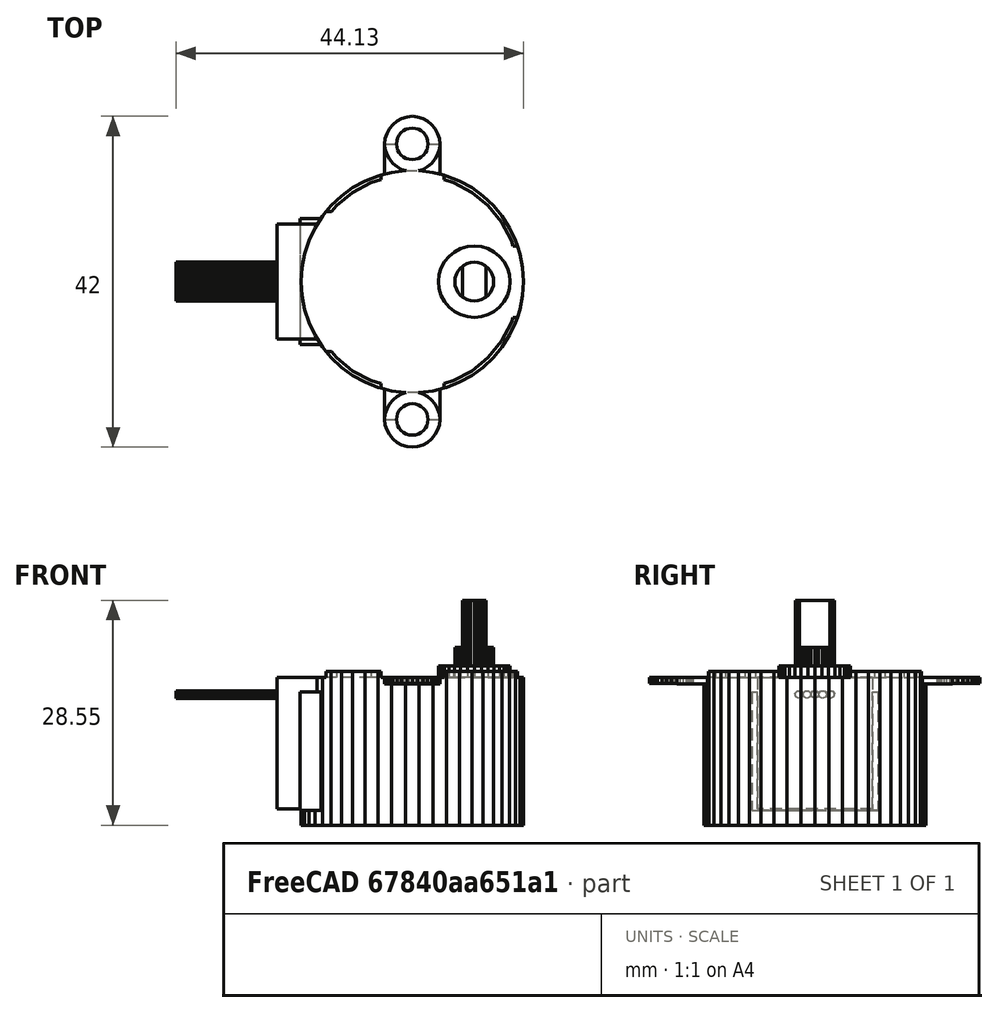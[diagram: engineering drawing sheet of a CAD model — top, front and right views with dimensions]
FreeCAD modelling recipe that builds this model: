
FCSTD DOCUMENT  (FreeCAD 0.14R3692 (Git))
Label: StepMotor_28BYJ-48
License: CC-BY 3.0
LicenseURL: http://creativecommons.org/licenses/by/3.0/
objects: Part::Prism×14, Part::Box×8, Part::MultiFuse×3, Part::Cut×3, Part::Fuse×3, Part::Feature×1
note: 32 computed .brp shape members not serialized (recipe doc carries the construction recipe); baked Part::Feature solids carry a one-line shape summary decoded from their .brp

FEATURE [Part::Prism] prism
  Circumradius = 14.125
  Height = 0.75
  Placement = pos=(0,0,-0.375) rot=(0,0,1;0rad)
  Polygon = 50
FEATURE [Part::Prism] prism001
  Circumradius = 13.625
  Height = 0.8
  Placement = pos=(0,0,-0.4) rot=(0,0,1;0rad)
  Polygon = 32
FEATURE [Part::Box] cube
  Height = 1.4
  Length = 8
  Placement = pos=(-4,-17.5,-0.7) rot=(0,0,1;0rad)
  Width = 35
FEATURE [Part::Box] cube001
  Height = 1.4
  Length = 30.25
  Placement = pos=(-15.125,-4.55,-0.7) rot=(0,0,1;0rad)
  Width = 9.1
FEATURE [Part::Box] cube002
  Height = 1.4
  Length = 28.25
  Placement = pos=(-28.25,-8.9,-0.7) rot=(0,0,1;0rad)
  Width = 17.8
FEATURE [Part::MultiFuse] union
  Shapes = -> [prism001,cube,cube001,cube002]
FEATURE [Part::Cut] difference
  Base = -> prism
  Placement = pos=(0,0,-9.75) rot=(0,0,1;0rad)
  Tool = -> union
FEATURE [Part::Prism] prism002
  Circumradius = 14.125
  Height = 18.8
  Placement = pos=(0,0,-9.4) rot=(0,0,1;0rad)
  Polygon = 50
FEATURE [Part::Prism] prism003
  Circumradius = 4.55
  Height = 18.8
  Placement = pos=(7.875,0,-10.85) rot=(0,0,1;0rad)
  Polygon = 32
FEATURE [Part::Prism] prism004
  Circumradius = 2.465
  Height = 18.8
  Placement = pos=(0,0,-9.4) rot=(0,0,1;0rad)
  Polygon = 32
FEATURE [Part::Box] cube003
  Height = 6
  Length = 4.93
  Placement = pos=(1.5,-2.465,-9.425) rot=(0,0,1;0rad)
  Width = 4.93
FEATURE [Part::Box] cube004
  Height = 6
  Length = 4.93
  Placement = pos=(-6.43,-2.465,-9.425) rot=(0,0,1;0rad)
  Width = 4.93
FEATURE [Part::Fuse] union001
  Base = -> cube003
  Tool = -> cube004
FEATURE [Part::Cut] difference001
  Base = -> prism004
  Placement = pos=(7.875,0,-9.75) rot=(0,0,1;0rad)
  Tool = -> union001
FEATURE [Part::Box] cube005
  Height = 0.8
  Length = 7
  Placement = pos=(-3.5,-17.5,-9.375) rot=(0,0,1;0rad)
  Width = 35
FEATURE [Part::Prism] prism005
  Circumradius = 3.5
  Height = 0.8
  Placement = pos=(0,17.5,-9.4) rot=(0,0,1;0rad)
  Polygon = 32
FEATURE [Part::Prism] prism006
  Circumradius = 3.5
  Height = 0.8
  Placement = pos=(0,-17.5,-9.4) rot=(0,0,1;0rad)
  Polygon = 32
FEATURE [Part::Box] cube006
  Height = 16.7
  Length = 28.25
  Placement = pos=(-17.175,-7.3,-9.35) rot=(0,0,1;0rad)
  Width = 14.6
FEATURE [Part::Box] cube007
  Height = 15
  Length = 24.5
  Placement = pos=(-14.25,-8,-7.5) rot=(0,0,1;0rad)
  Width = 16
FEATURE [Part::MultiFuse] union002
  Shapes = -> [difference,prism002,prism003,difference001,cube005,prism005,prism006,cube006,cube007]
FEATURE [Part::Prism] prism007
  Circumradius = 2
  Height = 2
  Placement = pos=(0,17.5,-10.4) rot=(0,0,1;0rad)
  Polygon = 32
FEATURE [Part::Prism] prism008
  Circumradius = 2
  Height = 2
  Placement = pos=(0,-17.5,-10.4) rot=(0,0,1;0rad)
  Polygon = 32
FEATURE [Part::Fuse] union003
  Base = -> prism007
  Tool = -> prism008
FEATURE [Part::Cut] difference002
  Base = -> union002
  Tool = -> union003
FEATURE [Part::Prism] prism009 .. prism013  x5 (patterned run collapsed; names and placements below)
  Circumradius = 0.5
  Height = 30
  Polygon = 7
  placements: 5 in arithmetic series — first pos=(0,2,0) rot=(0,0,1;0rad), step (0,-1,0), last pos=(0,-2,0) rot=(0,0,1;0rad)
FEATURE [Part::MultiFuse] Group
  Placement = pos=(0,0,-7.2) rot=(0,-1,0;1.5708rad)
  Shapes = -> [prism009,prism010,prism011,prism012,prism013]
FEATURE [Part::Fuse] Matrix_Union
  Base = -> difference002
  Placement = pos=(0,0,0) rot=(1,0,0;3.14159rad)
  Tool = -> Group
FEATURE [Part::Feature] Matrix_Union001  label="StepMotor_28BYJ-48"
  Placement = pos=(0,0,0) rot=(1,0,0;3.14159rad)
  shape: bbox 44.13 x 42 x 28.55 mm, 425 faces (baked)
